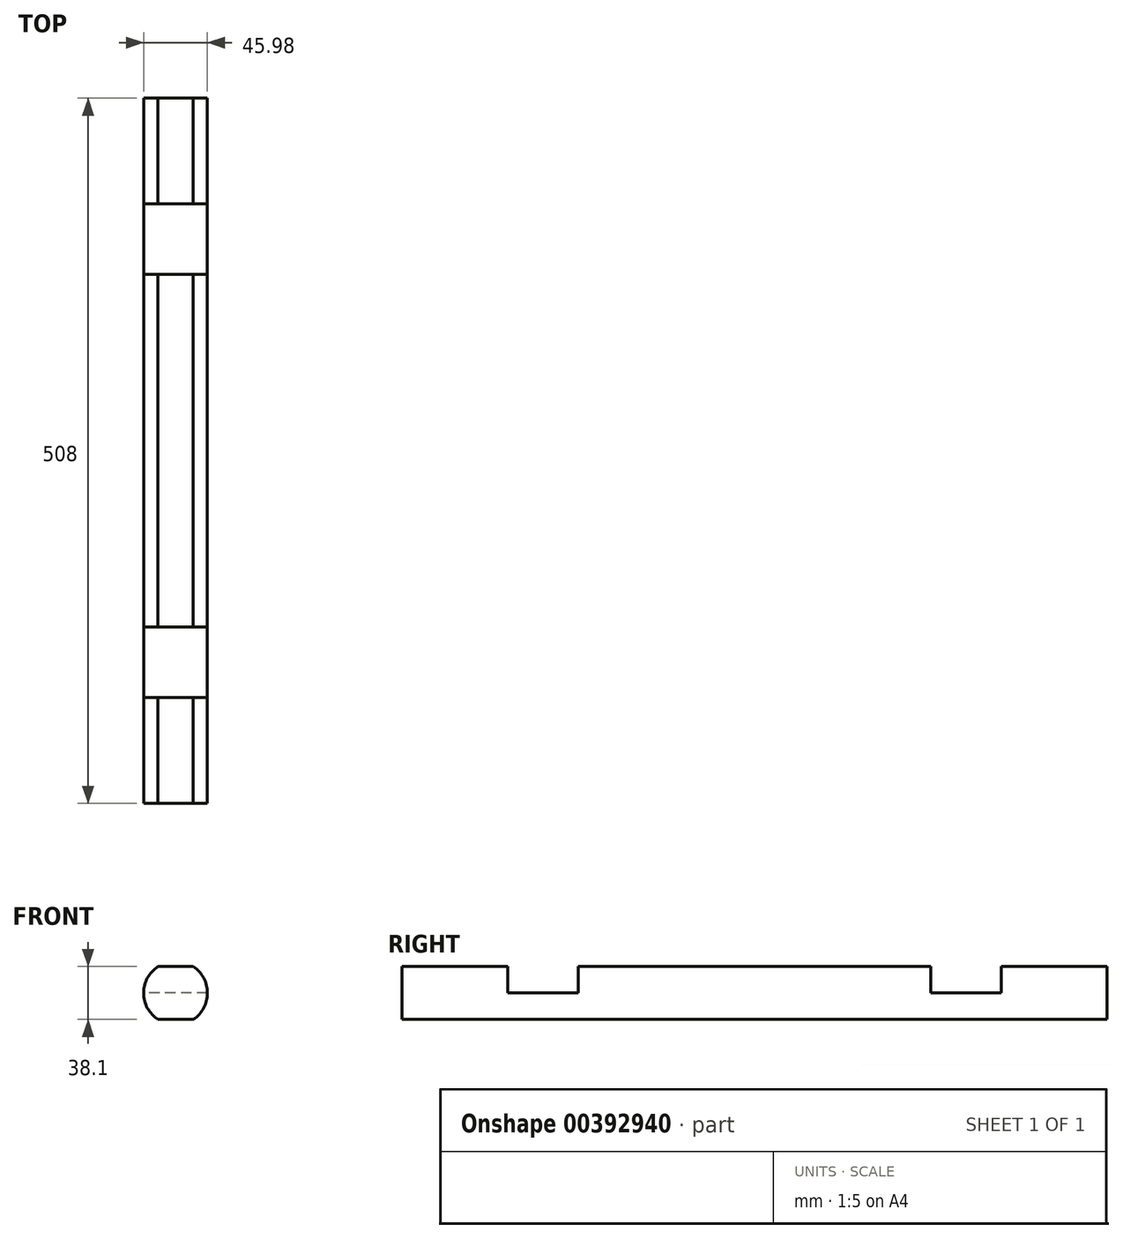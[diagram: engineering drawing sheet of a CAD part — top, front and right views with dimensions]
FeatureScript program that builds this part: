
annotation { "Feature Type Name" : "Feature", "Feature Type Description" : "" }
export const myFeature = defineFeature(function(context is Context, id is Id, definition is map)
    precondition{}
    {
        {
            var Q0;
            Q0=qCreatedBy(makeId("Front.planeOp"),FACE);
            var sketch = newSketch(context, id + "F0", { "sketchPlane" : qUnion([Q0])});
            skLineSegment(sketch, "E0", {"start": v(-21.85, 42.5) * mm, "end": v(3.55, 42.5) * mm});
            skLineSegment(sketch, "E1", {"start": v(-21.85, 4.4) * mm, "end": v(3.55, 4.4) * mm});
            skArc(sketch, "E2", {"start": v(-21.85, 42.5) * mm, "mid": v(-32.27, 23.45) * mm, "end": v(-21.85, 4.4) * mm});
            skArc(sketch, "E3", {"start": v(3.55, 4.4) * mm, "mid": v(13.71, 23.45) * mm, "end": v(3.55, 42.5) * mm});
            skSolve(sketch);
        }
        {
            var Q0;
            Q0 = qSketchRegion(id + "F0", true);
            extrude(context, id + "F1", {"entities" : qUnion([Q0]), "depth" : 508 * mm});
        }
        {
            var Q0;
            Q0=makeQuery(id+"F1.opExtrude","SWEPT_FACE",FACE,{"disambiguationData":[OSD([sQuery(id+"F0.wireOp",EDGE,"E0")])]});
            var sketch = newSketch(context, id + "F2", { "sketchPlane" : qUnion([Q0])});
            skLineSegment(sketch, "E4.bottom", {"start": v(-49.32, -431.8) * mm, "end": v(31.02, -431.8) * mm});
            skLineSegment(sketch, "E4.top", {"start": v(-49.32, -381) * mm, "end": v(31.02, -381) * mm});
            skLineSegment(sketch, "E4.left", {"start": v(-49.32, -431.8) * mm, "end": v(-49.32, -381) * mm});
            skLineSegment(sketch, "E4.right", {"start": v(31.02, -431.8) * mm, "end": v(31.02, -381) * mm});
            skPoint(sketch, "E4.middle", {"position": v(-9.15, -406.4) * mm});
            skPoint(sketch, "E4.middle.positionSnap0", {"position": v(-9.15, -508) * mm});
            skPoint(sketch, "E4.centerSnap0", {"position": v(-9.15, -508) * mm});
            skLineSegment(sketch, "E5.bottom", {"start": v(32.29, -127) * mm, "end": v(-50.58, -127) * mm});
            skLineSegment(sketch, "E5.top", {"start": v(32.29, -76.2) * mm, "end": v(-50.58, -76.2) * mm});
            skLineSegment(sketch, "E5.left", {"start": v(32.29, -127) * mm, "end": v(32.29, -76.2) * mm});
            skLineSegment(sketch, "E5.right", {"start": v(-50.58, -127) * mm, "end": v(-50.58, -76.2) * mm});
            skPoint(sketch, "E5.middle", {"position": v(-9.15, -101.6) * mm});
            skPoint(sketch, "E5.middle.positionSnap0", {"position": v(-9.15, 0) * mm});
            skPoint(sketch, "E5.centerSnap0", {"position": v(-9.15, 0) * mm});
            skSolve(sketch);
        }
        {
            var Q0;
            Q0 = qSketchRegion(id + "F2", true);
            extrude(context, id + "F3", {"entities" : qUnion([Q0]), "operationType" : NewBodyOperationType.REMOVE, "oppositeDirection" : true, "depth" : 19.05 * mm});
        }
    });
